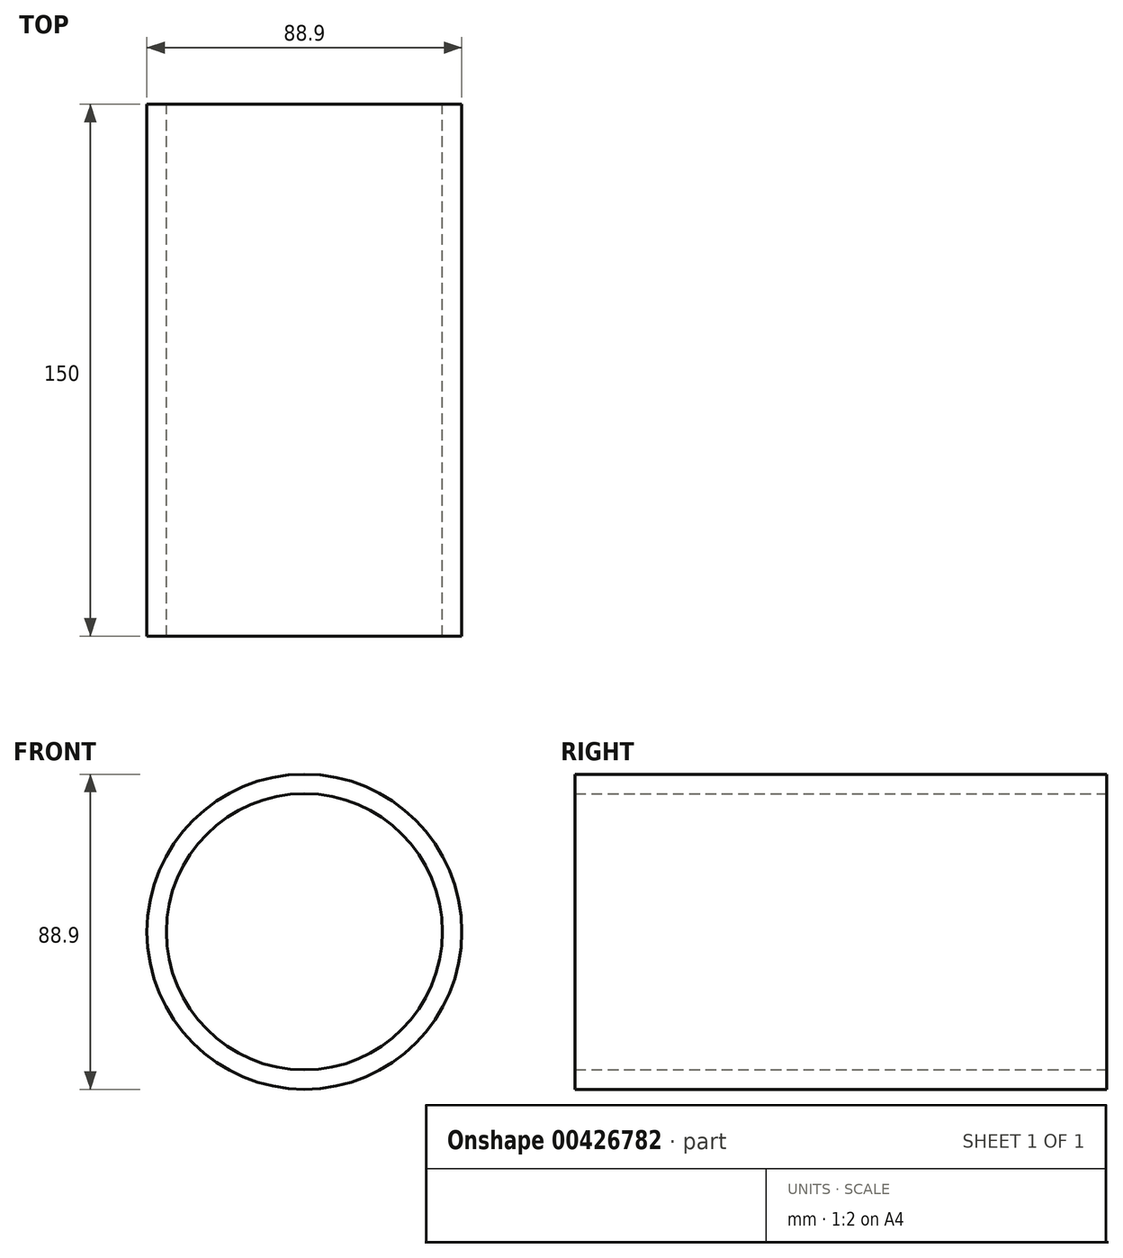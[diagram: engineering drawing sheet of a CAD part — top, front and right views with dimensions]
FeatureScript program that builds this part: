
annotation { "Feature Type Name" : "Feature", "Feature Type Description" : "" }
export const myFeature = defineFeature(function(context is Context, id is Id, definition is map)
    precondition{}
    {
        {
            var Q0;
            Q0=qCreatedBy(makeId("Front.planeOp"),FACE);
            var sketch = newSketch(context, id + "F0", { "sketchPlane" : qUnion([Q0])});
            skCircle(sketch, "E0", {"center": v(0, 0) * mm, "radius": 44.45 * mm});
            skCircle(sketch, "E1.0", {"center": v(0, 0) * mm, "radius": 38.96 * mm});
            skSolve(sketch);
        }
        {
            var Q0;
            Q0=makeQuery(id+"F0.imprint","IMPRINT",FACE,{"disambiguationData":[TD([[makeQuery(id+"F0.imprint","IMPRINT",EDGE,{"derivedFrom":sQuery(id+"F0.wireOp",EDGE,"E0")}),1.0]])]});
            extrude(context, id + "F1", {"entities" : qUnion([Q0]), "depth" : 150 * mm});
        }
    });
